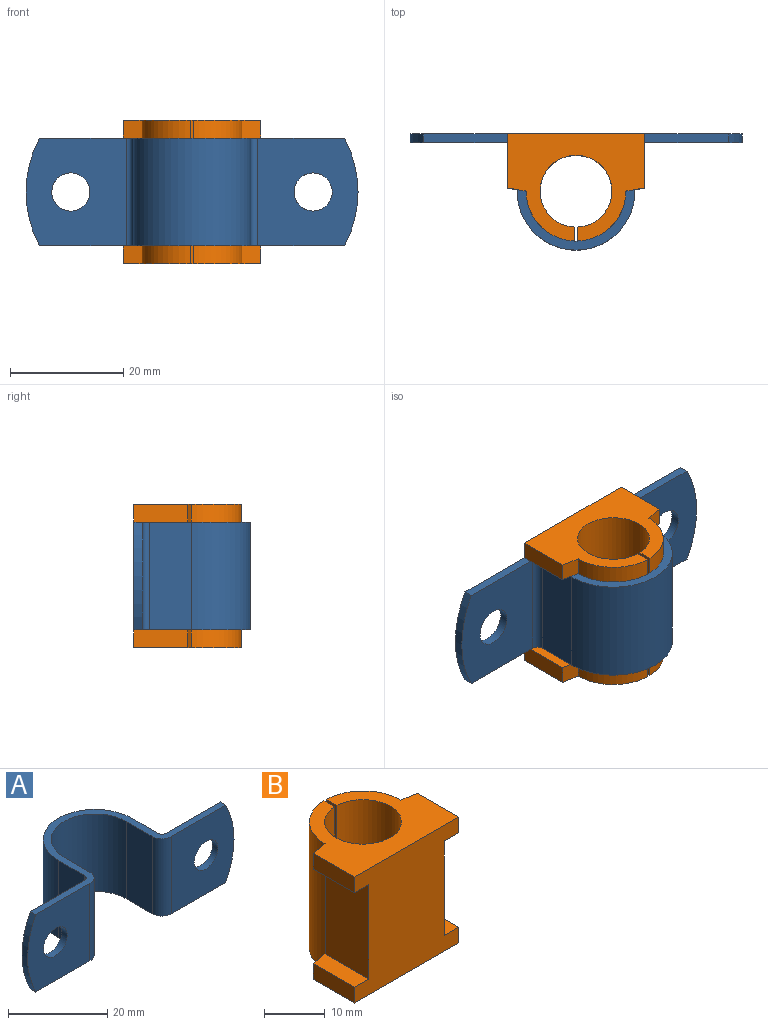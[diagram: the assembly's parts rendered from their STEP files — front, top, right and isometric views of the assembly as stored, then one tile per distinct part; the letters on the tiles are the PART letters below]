
ASSEMBLY  parts=2 mates=1
PART A: 20 faces, bbox 58.7x20.6x19.1 mm
  f0: plane 19.05x17.75mm, normal (0,-1,0), area 287.7mm2, adj f4,f5,f6,f17,f18
  f1: plane 19.05x17.75mm, normal (0,1,0), area 287.7mm2, adj f4,f5,f7,f17,f18
  f2: plane 19.05x17.75mm, normal (0,1,0), area 287.7mm2, adj f4,f5,f11,f16,f19
  f3: plane 19.05x17.75mm, normal (0,-1,0), area 287.7mm2, adj f4,f5,f12,f16,f19
  f4: plane 53.96x20.57mm, normal (0,0,1), area 130.1mm2, adj f0,f1,f2,f3,f6,f7,f8,f9
  f5: plane 53.96x20.57mm, normal (0,0,-1), area 130.1mm2, adj f0,f1,f2,f3,f6,f7,f8,f9
  f6: cylinder r=2.78mm len=19.05mm, axis (0,0,-1), area 83.1mm2, adj f0,f4,f5,f15
  f7: cylinder r=1.19mm len=19.05mm, axis (0,0,-1), area 35.6mm2, adj f1,f4,f5,f8
  f8: plane 19.05x7.38mm, normal (1,0,0), area 140.6mm2, adj f4,f5,f7,f9
  f9: cylinder r=10.41mm len=20.83mm, axis (0,0,-1), area 623.3mm2, adj f4,f5,f8,f10
  f10: plane 19.05x7.38mm, normal (-1,0,0), area 140.6mm2, adj f4,f5,f9,f11
  f11: cylinder r=1.19mm len=19.05mm, axis (0,0,-1), area 35.6mm2, adj f2,f4,f5,f10
  f12: cylinder r=2.78mm len=19.05mm, axis (0,0,-1), area 83.1mm2, adj f3,f4,f5,f13
  f13: plane 19.05x7.38mm, normal (1,0,0), area 140.6mm2, adj f4,f5,f12,f14
  f14: cylinder r=8.83mm len=19.05mm, axis (0,0,-1), area 528.2mm2, adj f4,f5,f13,f15
  f15: plane 19.05x7.38mm, normal (-1,0,0), area 140.6mm2, adj f4,f5,f6,f14
  f16: cylinder r=3.37mm len=6.75mm, axis (0,-1,0), area 33.6mm2, adj f2,f3
  f17: cylinder r=3.37mm len=6.75mm, axis (0,-1,0), area 33.6mm2, adj f0,f1
  f18: cylinder r=20.24mm len=19.05mm, axis (0,-1,0), area 31.5mm2, adj f0,f1,f4,f5
  f19: cylinder r=20.24mm len=19.05mm, axis (0,-1,0), area 31.5mm2, adj f2,f3,f4,f5
PART B: 22 faces, bbox 24.3x19x25.4 mm
  f0: cylinder r=8.83mm len=25.4mm, axis (0,0,-1), area 345.7mm2, adj f4,f7,f12,f13,f16,f21
  f1: plane 25.4x24.26mm, normal (0,-1,0), area 490.3mm2, adj f2,f5,f8,f9,f12,f13,f14,f15
  f2: plane 9.58x3.18mm, normal (1,0,0), area 30.4mm2, adj f1,f3,f12,f17
  f3: plane 3.3x3.18mm, normal (0.17,0.98,0), area 10.6mm2, adj f2,f6,f12,f17
  f4: plane 3.3x3.18mm, normal (-0.17,0.98,0), area 10.6mm2, adj f0,f5,f12,f14
  f5: plane 9.58x3.18mm, normal (-1,0,0), area 30.4mm2, adj f1,f4,f12,f14
  f6: cylinder r=8.83mm len=25.4mm, axis (0,0,-1), area 345.7mm2, adj f3,f10,f12,f13,f19,f20
  f7: plane 3.3x3.18mm, normal (-0.17,0.98,0), area 10.6mm2, adj f0,f8,f13,f15
  f8: plane 9.58x3.18mm, normal (-1,0,0), area 30.4mm2, adj f1,f7,f13,f15
  f9: plane 9.58x3.18mm, normal (1,0,0), area 30.4mm2, adj f1,f10,f13,f18
  f10: plane 3.3x3.18mm, normal (0.17,0.98,0), area 10.6mm2, adj f6,f9,f13,f18
  f11: cylinder r=6.35mm len=25.4mm, axis (0,0,-1), area 1000.5mm2, adj f12,f13,f20,f21
  f12: plane 24.26x18.98mm, normal (0,0,1), area 239mm2, adj f0,f1,f2,f3,f4,f5,f6,f11
  f13: plane 24.26x18.98mm, normal (0,0,-1), area 239mm2, adj f0,f1,f6,f7,f8,f9,f10,f11
  f14: plane 10.16x3.3mm, normal (0,0,-1), area 32.6mm2, adj f1,f4,f5,f16
  f15: plane 10.16x3.3mm, normal (0,0,1), area 32.6mm2, adj f1,f7,f8,f16
  f16: plane 19.05x10.16mm, normal (-1,0,0), area 193.5mm2, adj f0,f1,f14,f15
  f17: plane 10.16x3.3mm, normal (0,0,-1), area 32.6mm2, adj f1,f2,f3,f19
  f18: plane 10.16x3.3mm, normal (0,0,1), area 32.6mm2, adj f1,f9,f10,f19
  f19: plane 19.05x10.16mm, normal (1,0,0), area 193.5mm2, adj f1,f6,f17,f18
  f20: plane 25.4x2.48mm, normal (-1,0,0), area 62.9mm2, adj f6,f11,f12,f13
  f21: plane 25.4x2.48mm, normal (1,0,0), area 62.9mm2, adj f0,f11,f12,f13
PLACE A rot(axis=(1,0,0),180deg) t=(0,10.16,0)mm
PLACE B rot(axis=(1,0,0),180deg) t=(0,10.16,0)mm
MATE fastened A.f9 <-> B.f0  axis (0,0,1) through (0,0,0)mm
